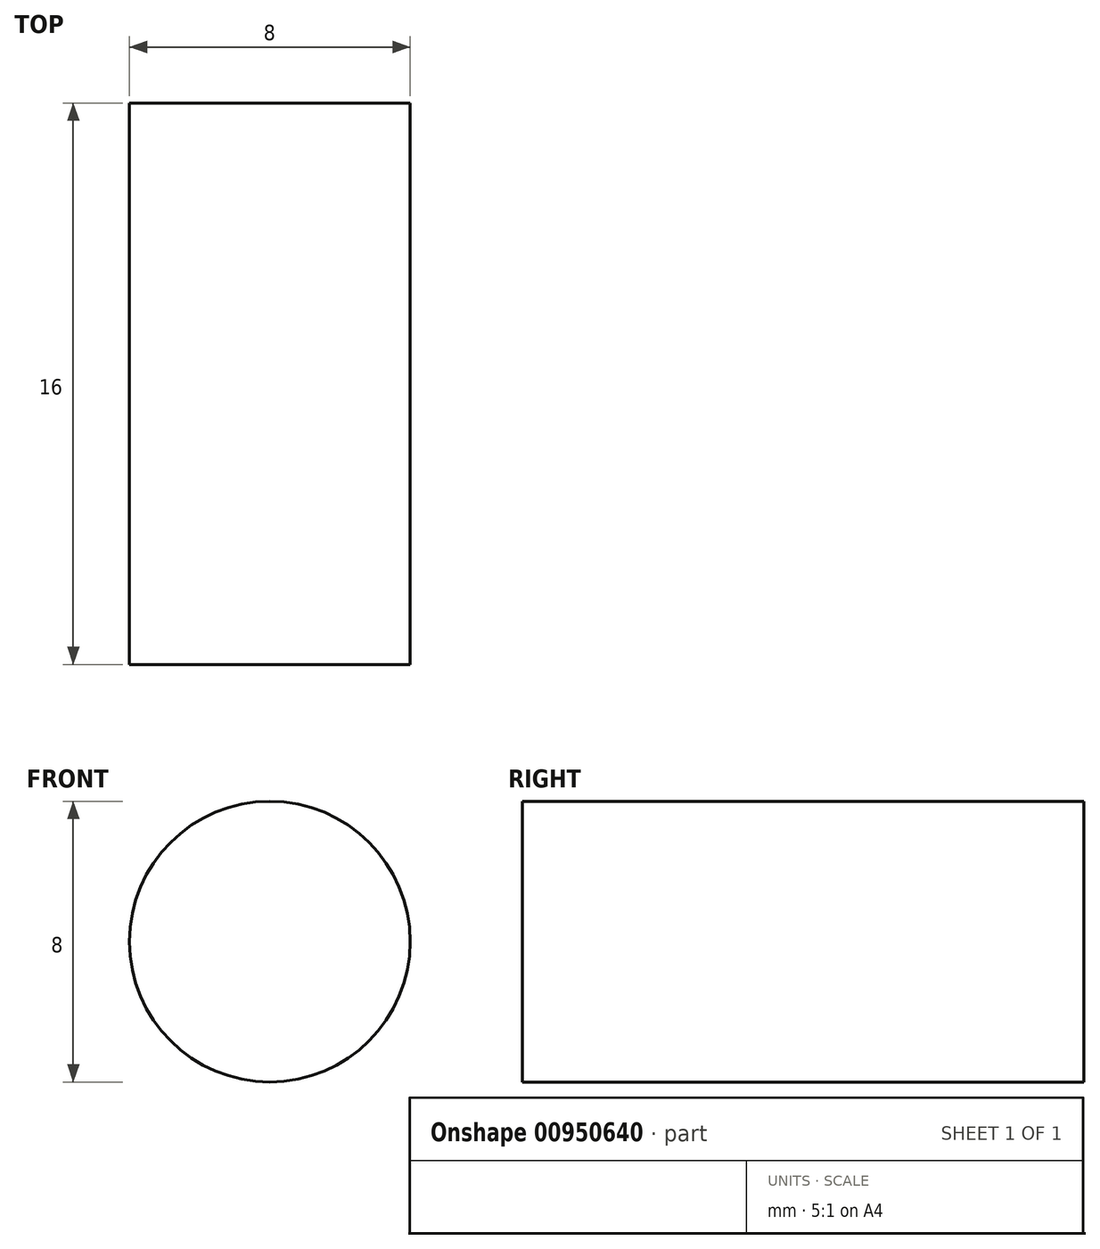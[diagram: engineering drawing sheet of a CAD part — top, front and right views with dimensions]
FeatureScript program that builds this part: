
annotation { "Feature Type Name" : "Feature", "Feature Type Description" : "" }
export const myFeature = defineFeature(function(context is Context, id is Id, definition is map)
    precondition{}
    {
        {
            var Q0;
            Q0=qCreatedBy(makeId("Front.planeOp"),FACE);
            var sketch = newSketch(context, id + "F0", { "sketchPlane" : qUnion([Q0])});
            skCircle(sketch, "E0", {"center": v(0, 0) * mm, "radius": 4 * mm});
            skSolve(sketch);
        }
        {
            var Q0;
            Q0 = qSketchRegion(id + "F0", true);
            extrude(context, id + "F1", {"entities" : qUnion([Q0]), "depth" : 16 * mm, "offsetDistance" : 25 * mm});
        }
    });
